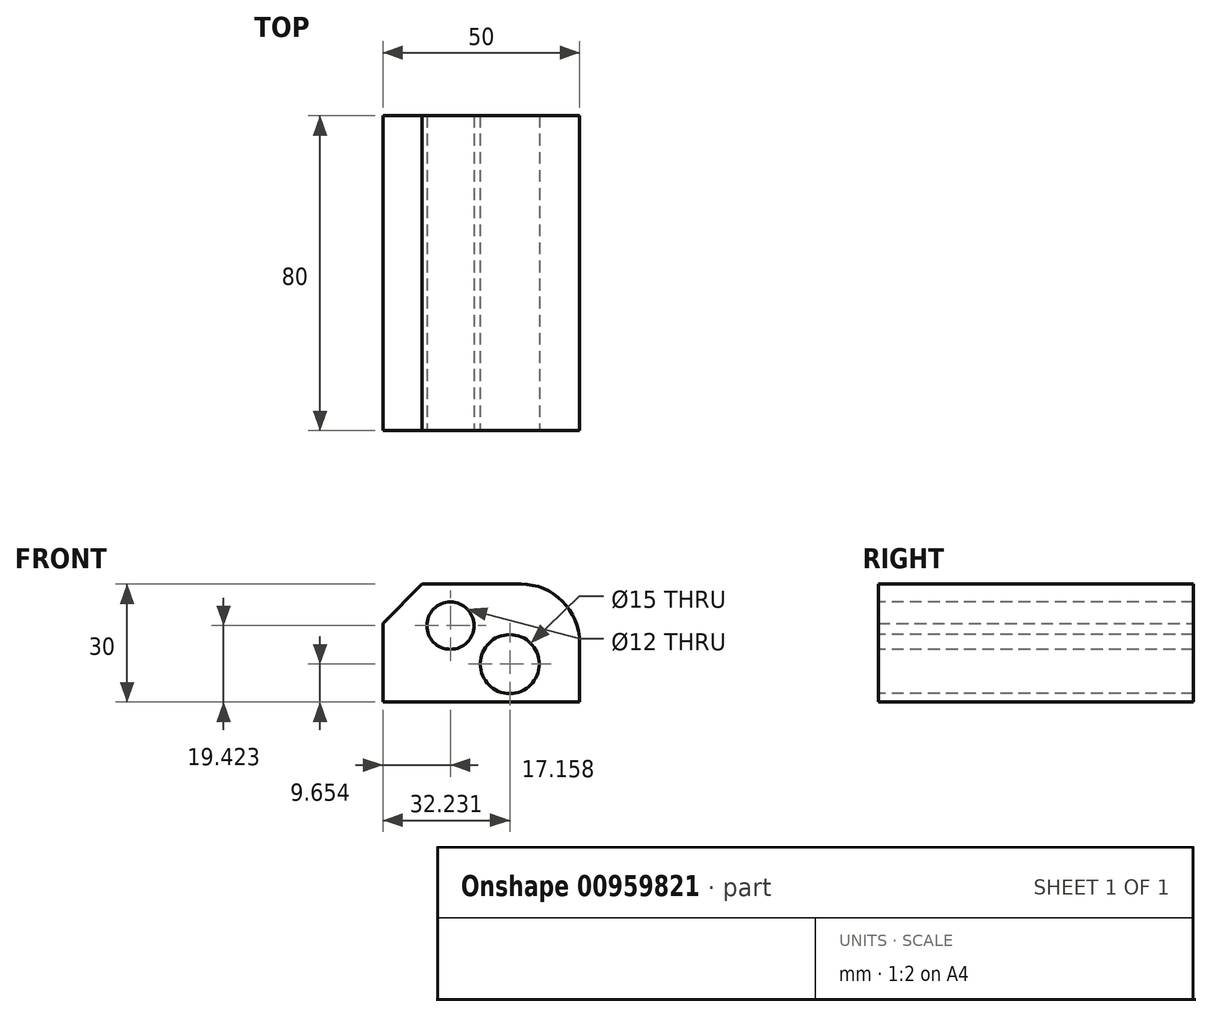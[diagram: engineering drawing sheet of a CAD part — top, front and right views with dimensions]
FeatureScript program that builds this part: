
annotation { "Feature Type Name" : "Feature", "Feature Type Description" : "" }
export const myFeature = defineFeature(function(context is Context, id is Id, definition is map)
    precondition{}
    {
        {
            var Q0;
            Q0=qCreatedBy(makeId("Top.planeOp"),FACE);
            var sketch = newSketch(context, id + "F0", { "sketchPlane" : qUnion([Q0])});
            skLineSegment(sketch, "E0.bottom", {"start": v(0, 0) * mm, "end": v(50, 0) * mm});
            skLineSegment(sketch, "E0.top", {"start": v(0, -80) * mm, "end": v(50, -80) * mm});
            skLineSegment(sketch, "E0.left", {"start": v(0, 0) * mm, "end": v(0, -80) * mm});
            skLineSegment(sketch, "E0.right", {"start": v(50, 0) * mm, "end": v(50, -80) * mm});
            skSolve(sketch);
        }
        {
            var Q0;
            Q0 = qSketchRegion(id + "F0", true);
            extrude(context, id + "F1", {"entities" : qUnion([Q0]), "depth" : 30 * mm, "offsetDistance" : 25 * mm});
        }
        {
            var Q0;
            Q0=makeQuery(id+"F1.opExtrude","CAP_EDGE",EDGE,{"disambiguationData":[OSD([sQuery(id+"F0.wireOp",EDGE,"E0.right")])],"isStart":false});
            fillet(context, id + "F2", {"entities" : qUnion([Q0]), "radius" : 14.97 * mm, "tangentPropagation" : true, "allowEdgeOverflow" : false});
        }
        {
            var Q0;
            Q0=makeQuery(id+"F1.opExtrude","CAP_EDGE",EDGE,{"disambiguationData":[OSD([sQuery(id+"F0.wireOp",EDGE,"E0.left")])],"isStart":false});
            chamfer(context, id + "F3", {"entities" : qUnion([Q0]), "width" : 10 * mm, "tangentPropagation" : true});
        }
        {
            var Q0;
            Q0=makeQuery(id+"F1.opExtrude","SWEPT_FACE",FACE,{"disambiguationData":[OSD([sQuery(id+"F0.wireOp",EDGE,"E0.top")])]});
            var sketch = newSketch(context, id + "F4", { "sketchPlane" : qUnion([Q0])});
            skCircle(sketch, "E1", {"center": v(17.16, 19.42) * mm, "radius": 6 * mm});
            skCircle(sketch, "E2", {"center": v(32.23, 9.65) * mm, "radius": 7.5 * mm});
            skSolve(sketch);
        }
        {
            var Q0;
            Q0 = qSketchRegion(id + "F4", true);
            extrude(context, id + "F5", {"entities" : qUnion([Q0]), "operationType" : NewBodyOperationType.REMOVE, "oppositeDirection" : true, "depth" : 80.8 * mm, "offsetDistance" : 25 * mm});
        }
    });
